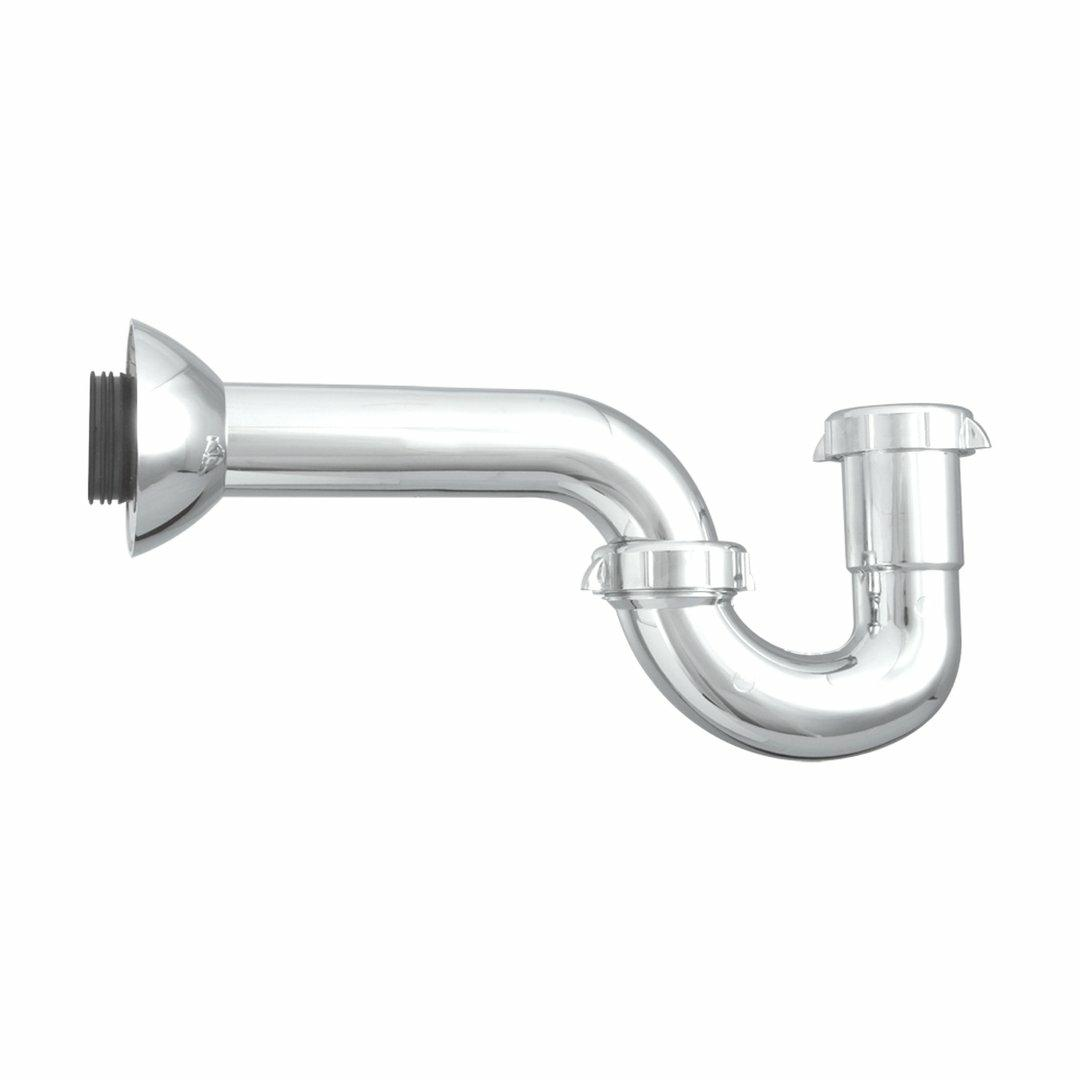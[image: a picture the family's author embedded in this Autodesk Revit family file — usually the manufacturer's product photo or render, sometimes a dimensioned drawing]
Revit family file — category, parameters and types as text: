
# Revit family: BIM_M1-3000-111
name_source: partatom
category: Aparatos sanitarios
units: mm (PartAtom-declared; Revit-internal decimal feet)

## family parameters
Activar corte en vistas = No
Anfitrión = Cara
Compartido = No
Corte con vacíos al cargar = No
Cota de conector redondo = Usar diámetro
Mantener orientación de anotación = No
Número OmniClass = 23.31.11.00
Punto de cálculo de habitación = No
Tipo de pieza = Normal

## types (1)
- M1-3000-111
    Acabado = Cepillado Brillante
    Alto = 155 mm  [stored 0.50853 ft]
    Ancho = 1000 mm  [stored 3.28084 ft]
    Conexión AC = Sí
    Conexión AF = Sí
    Conexión de residuos = No
    Conexión de ventilación = No
    Date Modified = 08-08-2025
    Descripción = Lavaplatos en acero
    Elevación por defecto = 0 mm  [stored 0 ft]
    Fabricante = Gricol
    Garantia Especifica = 5 años
    Imagen de tipo = FOTO LAVAPLATOS EN ACERO POCETA DERECHA 100 x 50 cm.jpg
    Largo = 500 mm  [stored 1.64042 ft]
    Link Ficha Tecnica = https://infotecnica.gricol.com
    Material = Acero inoxidable
    Modelo = M1-3000-111
    Nota clave = Perforación para griferia de 8 "
    Peso = 3.50 kg
    Product Name = Lavaplatos De Sobreponer Poceta Derecha 100 X 50 Cm Con Complementos Para Mezclador
    Resistencia a Corrosión = Si
    Sitio web = https://www.gricol.com
    Tipo de Uso = Residencial
    URL = https://www.gricol.com

note: [stored X ft] marks values corroborated as IEEE doubles in the binary element streams (Revit-internal decimal feet)

## geometry (parser evidence)
native form markers: Blend x2, Sweep x13
no freeform markers — native parametric forms only
